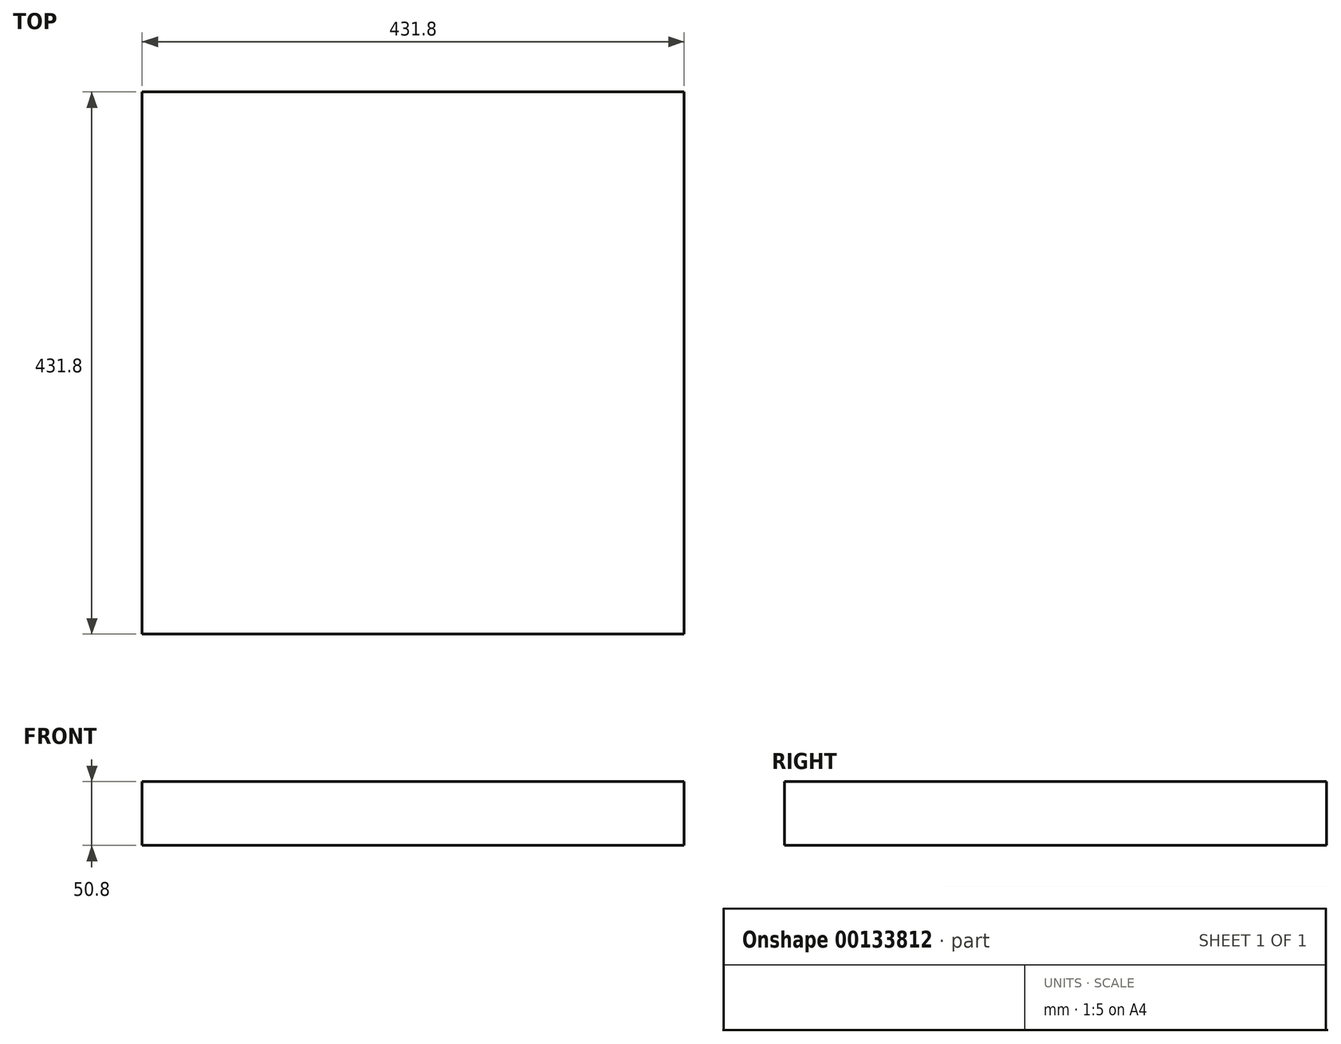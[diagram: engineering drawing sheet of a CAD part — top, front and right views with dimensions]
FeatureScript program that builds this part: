
annotation { "Feature Type Name" : "Feature", "Feature Type Description" : "" }
export const myFeature = defineFeature(function(context is Context, id is Id, definition is map)
    precondition{}
    {
        {
            var Q0;
            Q0=qCreatedBy(makeId("Top.planeOp"),FACE);
            var sketch = newSketch(context, id + "F0", { "sketchPlane" : qUnion([Q0])});
            skLineSegment(sketch, "E0.bottom", {"start": v(215.9, -215.9) * mm, "end": v(-215.9, -215.9) * mm});
            skLineSegment(sketch, "E0.top", {"start": v(215.9, 215.9) * mm, "end": v(-215.9, 215.9) * mm});
            skLineSegment(sketch, "E0.left", {"start": v(215.9, -215.9) * mm, "end": v(215.9, 215.9) * mm});
            skLineSegment(sketch, "E0.right", {"start": v(-215.9, -215.9) * mm, "end": v(-215.9, 215.9) * mm});
            skPoint(sketch, "E0.middle", {"position": v(0, 0) * mm});
            skSolve(sketch);
        }
        {
            var Q0;
            Q0=makeQuery(id+"F0.imprint","IMPRINT",FACE,{"disambiguationData":[TD([[makeQuery(id+"F0.imprint","IMPRINT",EDGE,{"derivedFrom":sQuery(id+"F0.wireOp",EDGE,"E0.bottom")}),-1.0]])]});
            extrude(context, id + "F1", {"entities" : qUnion([Q0]), "depth" : 50.8 * mm});
        }
    });
